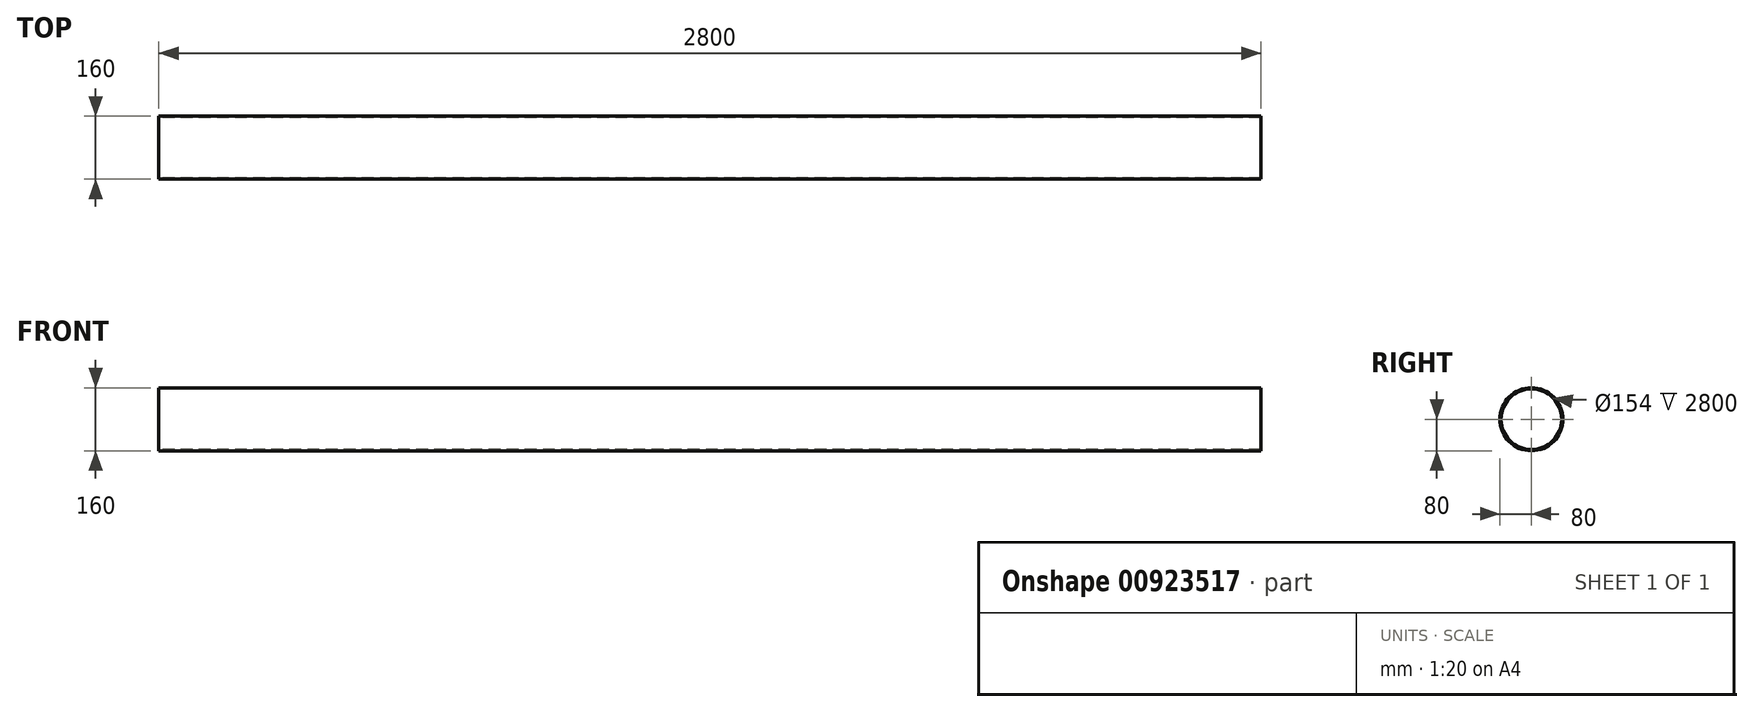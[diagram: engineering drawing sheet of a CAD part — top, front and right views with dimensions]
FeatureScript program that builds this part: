
annotation { "Feature Type Name" : "Feature", "Feature Type Description" : "" }
export const myFeature = defineFeature(function(context is Context, id is Id, definition is map)
    precondition{}
    {
        {
            var Q0;
            Q0=qCreatedBy(makeId("Right.planeOp"),FACE);
            var sketch = newSketch(context, id + "F0", { "sketchPlane" : qUnion([Q0])});
            skCircle(sketch, "E0", {"center": v(0, 0) * mm, "radius": 80 * mm});
            skCircle(sketch, "E1.0", {"center": v(0, 0) * mm, "radius": 77 * mm});
            skSolve(sketch);
        }
        {
            var Q0;
            Q0=makeQuery(id+"F0.imprint","IMPRINT",FACE,{"disambiguationData":[TD([[makeQuery(id+"F0.imprint","IMPRINT",EDGE,{"derivedFrom":sQuery(id+"F0.wireOp",EDGE,"E0")}),1.0]])]});
            extrude(context, id + "F1", {"entities" : qUnion([Q0]), "endBound" : BoundingType.SYMMETRIC, "depth" : 2800 * mm, "offsetDistance" : 25 * mm});
        }
    });
